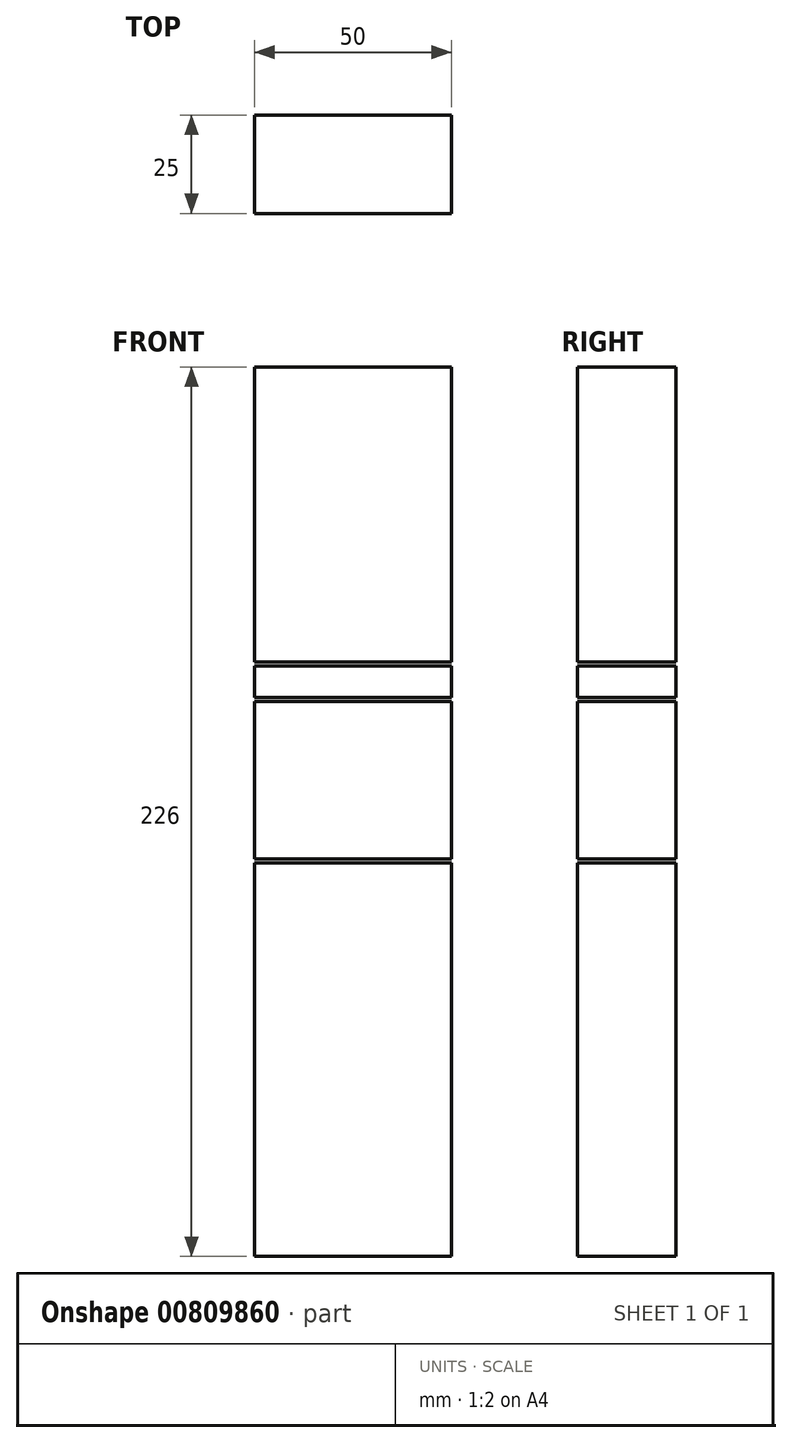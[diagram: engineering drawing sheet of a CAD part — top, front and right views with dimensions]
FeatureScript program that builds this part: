
annotation { "Feature Type Name" : "Feature", "Feature Type Description" : "" }
export const myFeature = defineFeature(function(context is Context, id is Id, definition is map)
    precondition{}
    {
        {
            var Q0;
            Q0=qCreatedBy(makeId("Front.planeOp"),FACE);
            var sketch = newSketch(context, id + "F0", { "sketchPlane" : qUnion([Q0])});
            skLineSegment(sketch, "E0.bottom", {"start": v(0, 0) * mm, "end": v(50, 0) * mm});
            skLineSegment(sketch, "E0.top", {"start": v(0, 100) * mm, "end": v(50, 100) * mm});
            skLineSegment(sketch, "E0.left", {"start": v(0, 0) * mm, "end": v(0, 100) * mm});
            skLineSegment(sketch, "E0.right", {"start": v(50, 0) * mm, "end": v(50, 100) * mm});
            skLineSegment(sketch, "E1.bottom", {"start": v(0, 101) * mm, "end": v(50, 101) * mm});
            skLineSegment(sketch, "E1.top", {"start": v(0, 141) * mm, "end": v(50, 141) * mm});
            skLineSegment(sketch, "E1.left", {"start": v(0, 101) * mm, "end": v(0, 141) * mm});
            skLineSegment(sketch, "E1.right", {"start": v(50, 101) * mm, "end": v(50, 141) * mm});
            skLineSegment(sketch, "E2.bottom", {"start": v(0, 142) * mm, "end": v(50, 142) * mm});
            skLineSegment(sketch, "E2.top", {"start": v(0, 150) * mm, "end": v(50, 150) * mm});
            skLineSegment(sketch, "E2.left", {"start": v(0, 142) * mm, "end": v(0, 150) * mm});
            skLineSegment(sketch, "E2.right", {"start": v(50, 142) * mm, "end": v(50, 150) * mm});
            skLineSegment(sketch, "E3.bottom", {"start": v(0, 151) * mm, "end": v(50, 151) * mm});
            skLineSegment(sketch, "E3.top", {"start": v(0, 226) * mm, "end": v(50, 226) * mm});
            skLineSegment(sketch, "E3.left", {"start": v(0, 151) * mm, "end": v(0, 226) * mm});
            skLineSegment(sketch, "E3.right", {"start": v(50, 151) * mm, "end": v(50, 226) * mm});
            skSolve(sketch);
        }
        {
            var Q0;
            Q0 = qSketchRegion(id + "F0", true);
            extrude(context, id + "F1", {"entities" : qUnion([Q0]), "oppositeDirection" : true, "depth" : 25 * mm, "offsetDistance" : 25 * mm});
        }
    });
